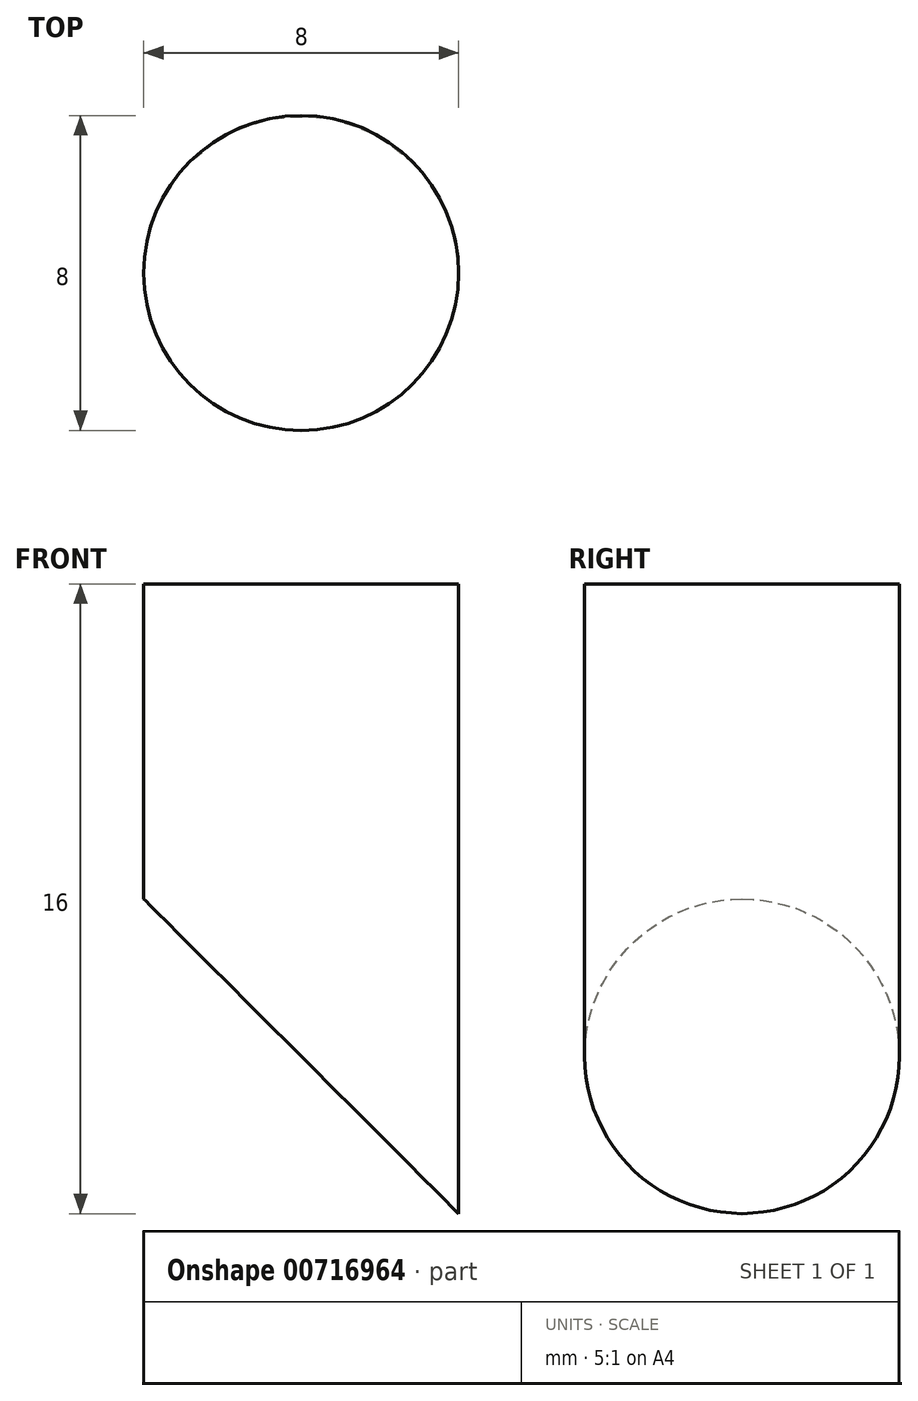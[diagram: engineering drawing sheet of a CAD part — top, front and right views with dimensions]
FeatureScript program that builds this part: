
annotation { "Feature Type Name" : "Feature", "Feature Type Description" : "" }
export const myFeature = defineFeature(function(context is Context, id is Id, definition is map)
    precondition{}
    {
        {
            var Q0;
            Q0=qCreatedBy(makeId("Front.planeOp"),FACE);
            var sketch = newSketch(context, id + "F0", { "sketchPlane" : qUnion([Q0])});
            skLineSegment(sketch, "E0.bottom", {"start": v(750, 10) * mm, "end": v(-750, 10) * mm});
            skLineSegment(sketch, "E0.top", {"start": v(750, -10) * mm, "end": v(-750, -10) * mm});
            skLineSegment(sketch, "E0.left", {"start": v(750, 10) * mm, "end": v(750, -10) * mm});
            skLineSegment(sketch, "E0.right", {"start": v(-750, 10) * mm, "end": v(-750, -10) * mm});
            skPoint(sketch, "E0.middle", {"position": v(0, 0) * mm});
            skSolve(sketch);
        }
        {
            var Q0;
            Q0=makeQuery(id+"F0.imprint","IMPRINT",FACE,{"disambiguationData":[TD([[makeQuery(id+"F0.imprint","IMPRINT",EDGE,{"derivedFrom":sQuery(id+"F0.wireOp",EDGE,"E0.bottom")}),1.0]])]});
            extrude(context, id + "F1", {"entities" : qUnion([Q0]), "depth" : (550 - 535) * mm, "offsetDistance" : 25 * mm});
        }
        {
            var Q0;
            Q0=makeQuery(id+"F1.opExtrude","CAP_FACE",FACE,{"disambiguationData":[OSD([sQuery(id+"F0.wireOp",EDGE,"E0.bottom"),sQuery(id+"F0.wireOp",EDGE,"E0.top"),sQuery(id+"F0.wireOp",EDGE,"E0.left"),sQuery(id+"F0.wireOp",EDGE,"E0.right")])],"isStart":true});
            var sketch = newSketch(context, id + "F2", { "sketchPlane" : qUnion([Q0])});
            skLineSegment(sketch, "E1", {"start": v(-750, -10) * mm, "end": v(-736, 4) * mm, "construction": true});
            skLineSegment(sketch, "E2", {"start": v(-736, 4) * mm, "end": v(736, 4) * mm, "construction": true});
            skLineSegment(sketch, "E3", {"start": v(736, 4) * mm, "end": v(750, -10) * mm, "construction": true});
            skLineSegment(sketch, "E4", {"start": v(750, -10) * mm, "end": v(-750, -10) * mm, "construction": true});
            skLineSegment(sketch, "E5", {"start": v(0, -10) * mm, "end": v(0, 119.19) * mm, "construction": true});
            skLineSegment(sketch, "E6", {"start": v(-750, -10) * mm, "end": v(-736, 4) * mm});
            skLineSegment(sketch, "E7", {"start": v(736, 4) * mm, "end": v(-736, 4) * mm});
            skLineSegment(sketch, "E8", {"start": v(-750, -10) * mm, "end": v(750, -10) * mm});
            skLineSegment(sketch, "E9", {"start": v(736, 4) * mm, "end": v(750, -10) * mm});
            skSolve(sketch);
        }
        {
            var Q0;
            Q0 = qSketchRegion(id + "F2", true);
            extrude(context, id + "F3", {"entities" : qUnion([Q0]), "operationType" : NewBodyOperationType.REMOVE, "oppositeDirection" : true, "depth" : 25 * mm, "offsetDistance" : 25 * mm});
        }
        {
            var Q0;
            Q0=makeQuery(id+"F1.opExtrude","CAP_FACE",FACE,{"disambiguationData":[OSD([sQuery(id+"F0.wireOp",EDGE,"E0.bottom"),sQuery(id+"F0.wireOp",EDGE,"E0.top"),sQuery(id+"F0.wireOp",EDGE,"E0.left"),sQuery(id+"F0.wireOp",EDGE,"E0.right")])],"isStart":true});
            var sketch = newSketch(context, id + "F4", { "sketchPlane" : qUnion([Q0])});
            skLineSegment(sketch, "E10.bottom", {"start": v(-750, 10) * mm, "end": v(750, 10) * mm});
            skLineSegment(sketch, "E10.top", {"start": v(-750, -10) * mm, "end": v(750, -10) * mm});
            skLineSegment(sketch, "E10.left", {"start": v(-750, 10) * mm, "end": v(-750, -10) * mm});
            skLineSegment(sketch, "E10.right", {"start": v(750, 10) * mm, "end": v(750, -10) * mm});
            skSolve(sketch);
        }
        {
            var Q0;
            Q0 = qSketchRegion(id + "F4", true);
            extrude(context, id + "F5", {"entities" : qUnion([Q0]), "operationType" : NewBodyOperationType.ADD, "depth" : 4 * mm, "offsetDistance" : 25 * mm});
        }
        {
            var Q0;
            Q0=makeQuery(id+"F5.boolean.opBoolean","MERGE",FACE,{"derivedFrom":[makeQuery(id+"F1.opExtrude","SWEPT_FACE",FACE,{"disambiguationData":[OSD([sQuery(id+"F0.wireOp",EDGE,"E0.bottom")])]}),makeQuery(id+"F5.opExtrude","SWEPT_FACE",FACE,{"disambiguationData":[OSD([sQuery(id+"F4.wireOp",EDGE,"E10.bottom")])]})]});
            var sketch = newSketch(context, id + "F6", { "sketchPlane" : qUnion([Q0])});
            skCircle(sketch, "E11", {"center": v(-742, -5.5) * mm, "radius": 4 * mm});
            skLineSegment(sketch, "E12", {"start": v(-750, -5.5) * mm, "end": v(-742, -5.5) * mm, "construction": true});
            skLineSegment(sketch, "E13", {"start": v(-742, -5.5) * mm, "end": v(-742, -15) * mm, "construction": true});
            skLineSegment(sketch, "E14", {"start": v(0, 0) * mm, "end": v(0, -127.93) * mm, "construction": true});
            skCircle(sketch, "E15.MirrorC", {"center": v(742, -5.5) * mm, "radius": 4 * mm});
            skSolve(sketch);
        }
        {
            var Q0;
            Q0=makeQuery(id+"F6.imprint","IMPRINT",FACE,{"disambiguationData":[TD([[makeQuery(id+"F6.imprint","IMPRINT",EDGE,{"derivedFrom":sQuery(id+"F6.wireOp",EDGE,"E11")}),1.0]])]});
            var Q1;
            Q1=makeQuery(id+"F6.imprint","IMPRINT",FACE,{"disambiguationData":[TD([[makeQuery(id+"F6.imprint","IMPRINT",EDGE,{"derivedFrom":sQuery(id+"F6.wireOp",EDGE,"E15.MirrorC")}),-1.0]])]});
            extrude(context, id + "F7", {"entities" : qUnion([Q0, Q1]), "operationType" : NewBodyOperationType.REMOVE, "endBound" : BoundingType.THROUGH_ALL, "oppositeDirection" : true, "depth" : 25 * mm, "offsetDistance" : 25 * mm});
        }
    });
